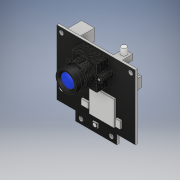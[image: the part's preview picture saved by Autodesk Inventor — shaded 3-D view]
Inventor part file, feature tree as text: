
AUTODESK INVENTOR PART (.ipt)
format: ipt  version: 2017 (Build 210142000, 142)  size: 619,520 bytes
history: native  units: in
note: dims shown in document units (in); Inventor stores cm internally (conversion verified against a paired STEP export)
features: sketch x24, extrude x22, projected_geometry x7, chamfer x4, pattern_linear x4, plane x2, revolve x2, fillet x2, mirror x1, other x1
ambient origin geometry x8: Origin, YZ Plane, XZ Plane, XY Plane, X Axis, Y Axis, Z Axis, Center Point
bodies: Solid1 (feature_tree)
feature tree (69):
  extrude  "Extrusion1"  Depth=1.75in
  extrude  "Extrusion2"  Depth=0.5in
  extrude  "Extrusion3"  Depth=0.125in
  extrude  "Extrusion4"  Depth=0.12in
  plane  "Work Plane1"
  revolve  "Revolution1"  [1 undecoded]
  extrude  "Extrusion5"  Depth=0.125in
  extrude  "Extrusion6"  Depth=0.15in
  extrude  "Extrusion7"  Depth=0.06in TaperAngle=0.0deg
  extrude  "Extrusion8"  Depth=0.67in
  extrude  "Extrusion9"  Depth=0.063in
  extrude  "Extrusion10"  Depth=0.06in
  plane  "Work Plane2"
  mirror  "Mirror1"
  extrude  "Extrusion11"  Depth=0.59in
  extrude  "Extrusion12"  Depth=0.0016in
  chamfer  "Chamfer1"  Distance=0.2598in
  extrude  "Extrusion13"  Depth=0.047in
  chamfer  "Chamfer2"  Distance=0.038in
  pattern_linear  "Rectangular Pattern1"  Spacing1=0.245in  [1 undecoded]
  extrude  "Extrusion14"  Depth=0.234in
  extrude  "Extrusion15"  Depth=0.234in
  fillet  "Fillet1"  Radius=0.284in
  extrude  "Extrusion16"  Depth=0.234in
  chamfer  "Chamfer3"  Distance=0.1225in
  pattern_linear  "Rectangular Pattern3"  Spacing1=0.135in  [1 undecoded]
  pattern_linear  "Rectangular Pattern4"  Spacing1=0.173in  [1 undecoded]
  extrude  "Extrusion17"  Depth=0.234in
  extrude  "Extrusion18"  Depth=0.234in
  chamfer  "Chamfer4"  Distance=0.369in
  pattern_linear  "Rectangular Pattern5"  Spacing1=0.018in  [1 undecoded]
  extrude  "Extrusion19"  Depth=0.234in
  extrude  "Extrusion20"  Depth=0.234in TaperAngle=0.0deg
  fillet  "Fillet2"  Radius=0.35in
  extrude  "Extrusion21"  Depth=0.234in
  extrude  "Extrusion22"  Depth=0.234in
  revolve  "Revolution2"  [1 undecoded]
  sketch  "Sketch1"  dims[d0=2.12in d1=1.75in]
  sketch  "Sketch2"  dims[d2=0.5in d3=0.5in]
  sketch  "Sketch3"  dims[d4=0.25in d5=0.125in]
  projected_geometry  "Projected Loop1"
  sketch  "Sketch4"  dims[d6=0.125in d7=0.12in]
  projected_geometry  "Projected Loop2"
  other  "Work Axis1"
  sketch  "Sketch5"  dims[d8=0.125in d9=0.12in]
  projected_geometry  "Projected Loop3"
  sketch  "Sketch6"  dims[d10=0.32in d11=0.125in]
  sketch  "Sketch7"  dims[d12=0.15in d13=0.15in]
  sketch  "Sketch8"  dims[d14=0.125in d15=0.06in d16=0.0in]
  sketch  "Sketch9"  dims[d17=0.67in d18=0.175in]
  sketch  "Sketch10"  dims[d19=0.964in d20=0.063in]
  sketch  "Sketch11"  dims[d21=0.06in d22=0.335in]
  projected_geometry  "Projected Loop4"
  sketch  "Sketch12"  dims[d23=0.314in d24=0.0in d25=0.59in]
  sketch  "Sketch13"  dims[d26=0.115in d27=0.238in d28=0.0016in]
  projected_geometry  "Projected Loop5"
  sketch  "Sketch14"  dims[d29=0.552in d30=0.2598in d31=0.0in]
  sketch  "Sketch15"  dims[d32=0.0in d33=0.047in]
  projected_geometry  "Projected Loop6"
  sketch  "Sketch16"  dims[d34=0.096in]
  sketch  "Sketch17"  dims[d35=135.0deg]
  projected_geometry  "Projected Loop7"
  sketch  "Sketch18"  dims[d36=0.02in]
  sketch  "Sketch19"  dims[d37=90.0deg]
  sketch  "Sketch20"  dims[d38=0.1111in]
  sketch  "Sketch21"  dims[d39=0.138in]
  sketch  "Sketch22"  dims[d40=0.15in d41=0.038in d42=0.0in]
  sketch  "Sketch23"  dims[d43=0.104in]
  sketch  "Sketch24"  dims[d44=0.0001in d45=0.0in d46=0.245in d47=0.145in d48=0.407in d49=0.284in d50=0.0in d51=0.1225in d52=0.1225in d53=0.135in d54=0.173in d55=0.0in d56=0.158in d57=0.3in d58=0.369in d59=0.0in d60=0.018in d61=0.0543in d62=0.1in d63=0.0in d64=0.35in d65=0.8in d66=0.184in d67=0.049in d68=0.424in d69=0.0in d70=0.04in d71=0.174in d72=0.261in d73=0.0in d74=0.02in d75=0.125in d76=45.0deg d77=0.025in d78=0.05in d79=0.2in d80=0.24in d81=0.0in d82=0.01in d83=0.125in d84=45.0deg d85=1.9685in d87=0.1in d88=0.7874in d90=0.1in d91=0.015in d92=0.24in d93=0.0in d94=0.095in d95=0.193in d96=0.359in d97=0.323in d98=0.147in d99=0.0in d100=0.03in d104=0.05in d105=0.025in d106=0.233in d107=0.0in d108=0.01in d109=0.125in d110=45.0deg d111=0.7874in d113=0.1in d114=1.1811in d116=0.0951in d117=0.2in d118=0.051in d119=0.072in d120=0.0in d121=0.05in d122=0.025in d123=0.293in d124=0.0in d125=0.01in d126=0.125in d127=45.0deg d128=0.7874in d130=0.1in d131=0.205in d132=0.091in d133=0.105in d134=0.2in d135=0.036in d136=0.0in d137=0.135in d138=0.078in d139=0.036in d140=0.0in d141=0.03in d142=0.67in d143=0.19in d144=0.525in d145=0.196in d146=0.363in d147=0.126in d148=0.204in d149=0.15in d150=0.19in d151=0.704in d152=0.503in d153=0.05in d154=0.0in d155=0.235in d156=0.251in d157=0.254in d158=0.409in d159=0.091in d160=0.0in d161=0.118in d162=0.234in d163=90.0deg]
note: 6 required parameter values undecoded (feature->parameter linkage not recoverable at this tier; creation-order binding heuristic only, values carry confidence <= 0.55)